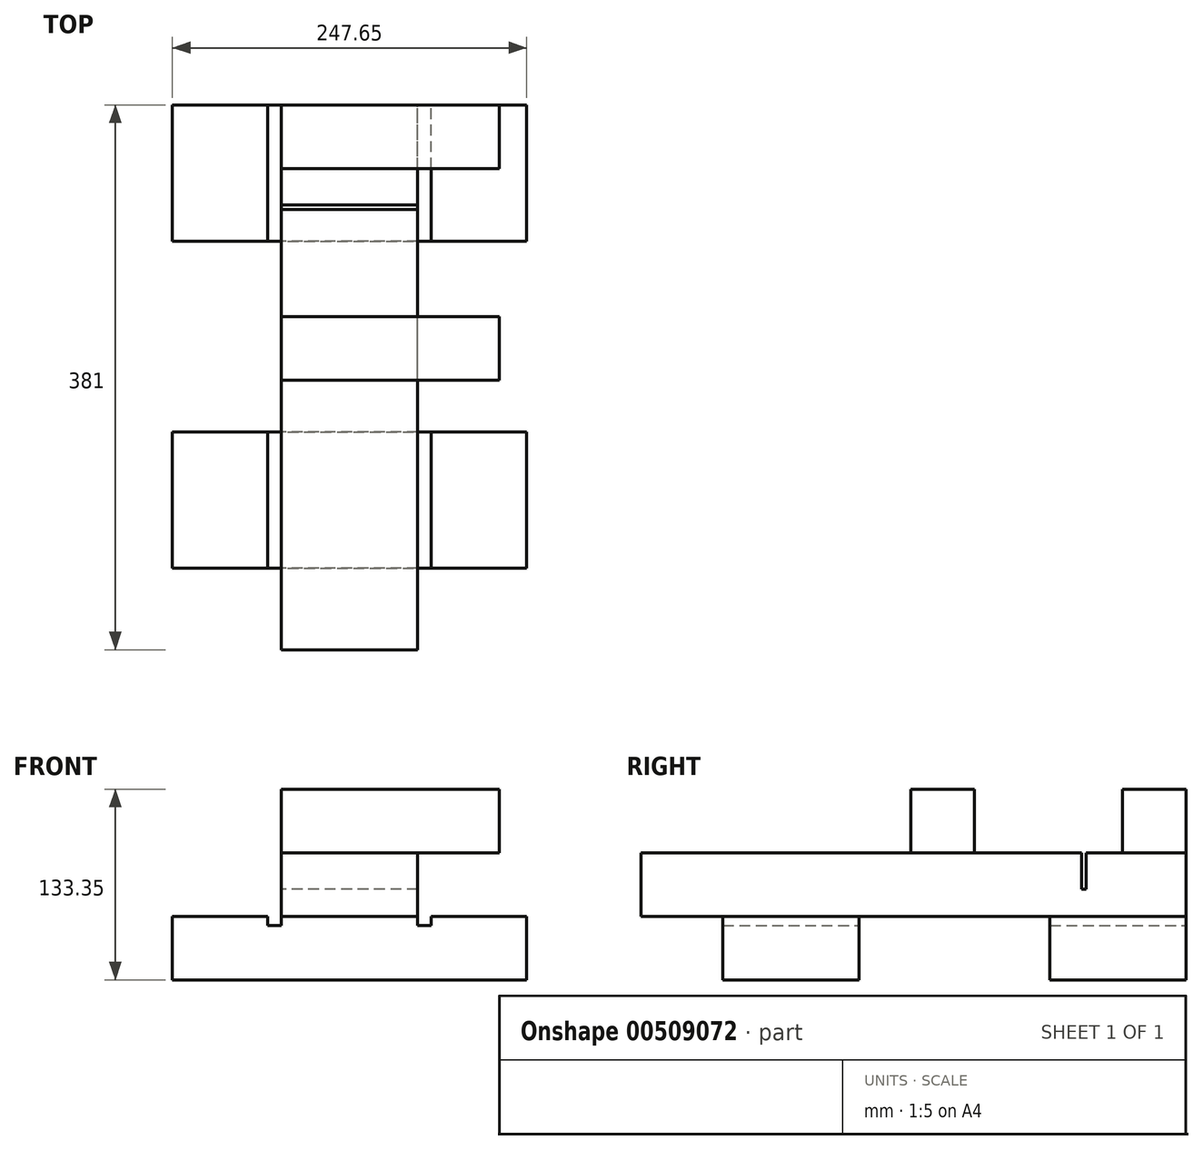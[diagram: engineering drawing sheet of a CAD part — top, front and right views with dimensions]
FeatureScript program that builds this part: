
annotation { "Feature Type Name" : "Feature", "Feature Type Description" : "" }
export const myFeature = defineFeature(function(context is Context, id is Id, definition is map)
    precondition{}
    {
        {
            var Q0;
            Q0=qCreatedBy(makeId("Front.planeOp"),FACE);
            var sketch = newSketch(context, id + "F0", { "sketchPlane" : qUnion([Q0])});
            skLineSegment(sketch, "E0.bottom", {"start": v(0, 0) * mm, "end": v(95.25, 0) * mm});
            skLineSegment(sketch, "E0.top", {"start": v(0, 44.45) * mm, "end": v(95.25, 44.45) * mm});
            skLineSegment(sketch, "E0.left", {"start": v(0, 0) * mm, "end": v(0, 44.45) * mm});
            skLineSegment(sketch, "E0.right", {"start": v(95.25, 0) * mm, "end": v(95.25, 44.45) * mm});
            skSolve(sketch);
        }
        {
            var Q0;
            Q0=makeQuery(id+"F0.imprint","IMPRINT",FACE,{"disambiguationData":[TD([[makeQuery(id+"F0.imprint","IMPRINT",EDGE,{"derivedFrom":sQuery(id+"F0.wireOp",EDGE,"E0.bottom")}),1.0]])]});
            extrude(context, id + "F1", {"entities" : qUnion([Q0]), "depth" : 381 * mm});
        }
        {
            var Q0;
            Q0=qCreatedBy(makeId("Front.planeOp"),FACE);
            var sketch = newSketch(context, id + "F2", { "sketchPlane" : qUnion([Q0])});
            skLineSegment(sketch, "E1", {"start": v(-9.52, 0) * mm, "end": v(-76.2, 0) * mm});
            skLineSegment(sketch, "E2", {"start": v(-76.2, 0) * mm, "end": v(-76.2, -44.45) * mm});
            skLineSegment(sketch, "E3", {"start": v(-76.2, -44.45) * mm, "end": v(171.45, -44.45) * mm});
            skLineSegment(sketch, "E4", {"start": v(171.45, -44.45) * mm, "end": v(171.45, 0) * mm});
            skLineSegment(sketch, "E5", {"start": v(171.45, 0) * mm, "end": v(104.78, 0) * mm});
            skLineSegment(sketch, "E6", {"start": v(104.78, 0) * mm, "end": v(104.78, -6.35) * mm});
            skLineSegment(sketch, "E7", {"start": v(104.78, -6.35) * mm, "end": v(95.25, -6.35) * mm});
            skLineSegment(sketch, "E8", {"start": v(95.25, -6.35) * mm, "end": v(95.25, 0) * mm});
            skLineSegment(sketch, "E9", {"start": v(95.25, 0) * mm, "end": v(0, 0) * mm});
            skLineSegment(sketch, "E10", {"start": v(0, 0) * mm, "end": v(0, -6.35) * mm});
            skLineSegment(sketch, "E11", {"start": v(0, -6.35) * mm, "end": v(-9.52, -6.35) * mm});
            skLineSegment(sketch, "E12", {"start": v(-9.52, -6.35) * mm, "end": v(-9.52, 0) * mm});
            skSolve(sketch);
        }
        {
            var Q0;
            Q0=makeQuery(id+"F2.imprint","IMPRINT",FACE,{"disambiguationData":[TD([[makeQuery(id+"F2.imprint","IMPRINT",EDGE,{"derivedFrom":sQuery(id+"F2.wireOp",EDGE,"E1")}),1.0]])]});
            extrude(context, id + "F3", {"entities" : qUnion([Q0]), "depth" : 95.25 * mm});
        }
        {
            var Q0;
            Q0=qCreatedBy(makeId("Front.planeOp"),FACE);
            cPlane(context, id + "F4", {"entities" : qUnion([Q0]), "cplaneType" : CPlaneType.OFFSET, "offset" : 228.6 * mm, "width" : 152.4 * mm, "height" : 152.4 * mm});
        }
        {
            var Q0;
            Q0=qCreatedBy(id+"F4.planeOp",FACE);
            var sketch = newSketch(context, id + "F5", { "sketchPlane" : qUnion([Q0])});
            skLineSegment(sketch, "E13", {"start": v(-9.53, 0) * mm, "end": v(-76.2, 0) * mm});
            skLineSegment(sketch, "E14", {"start": v(-76.2, 0) * mm, "end": v(-76.2, -44.45) * mm});
            skLineSegment(sketch, "E15", {"start": v(-76.2, -44.45) * mm, "end": v(171.45, -44.45) * mm});
            skLineSegment(sketch, "E16", {"start": v(171.45, -44.45) * mm, "end": v(171.45, 0) * mm});
            skLineSegment(sketch, "E17", {"start": v(171.45, 0) * mm, "end": v(104.78, 0) * mm});
            skLineSegment(sketch, "E18", {"start": v(104.78, 0) * mm, "end": v(104.78, -6.35) * mm});
            skLineSegment(sketch, "E19", {"start": v(104.78, -6.35) * mm, "end": v(95.25, -6.35) * mm});
            skLineSegment(sketch, "E20", {"start": v(95.25, -6.35) * mm, "end": v(95.25, 0) * mm});
            skLineSegment(sketch, "E21", {"start": v(95.25, 0) * mm, "end": v(0, 0) * mm});
            skLineSegment(sketch, "E22", {"start": v(0, 0) * mm, "end": v(0, -6.35) * mm});
            skLineSegment(sketch, "E23", {"start": v(0, -6.35) * mm, "end": v(-9.53, -6.35) * mm});
            skLineSegment(sketch, "E24", {"start": v(-9.53, -6.35) * mm, "end": v(-9.53, 0) * mm});
            skSolve(sketch);
        }
        {
            var Q0;
            Q0=makeQuery(id+"F5.imprint","IMPRINT",FACE,{"disambiguationData":[TD([[makeQuery(id+"F5.imprint","IMPRINT",EDGE,{"derivedFrom":sQuery(id+"F5.wireOp",EDGE,"E13")}),1.0]])]});
            extrude(context, id + "F6", {"entities" : qUnion([Q0]), "depth" : 95.25 * mm});
        }
        {
            var Q0;
            Q0=qCreatedBy(makeId("Right.planeOp"),FACE);
            var sketch = newSketch(context, id + "F7", { "sketchPlane" : qUnion([Q0])});
            skLineSegment(sketch, "E25.bottom", {"start": v(-192.53, 88.9) * mm, "end": v(-148.08, 88.9) * mm});
            skLineSegment(sketch, "E25.top", {"start": v(-192.53, 44.45) * mm, "end": v(-148.08, 44.45) * mm});
            skLineSegment(sketch, "E25.left", {"start": v(-192.53, 88.9) * mm, "end": v(-192.53, 44.45) * mm});
            skLineSegment(sketch, "E25.right", {"start": v(-148.08, 88.9) * mm, "end": v(-148.08, 44.45) * mm});
            skLineSegment(sketch, "E26.bottom", {"start": v(-44.45, 88.9) * mm, "end": v(0, 88.9) * mm});
            skLineSegment(sketch, "E26.top", {"start": v(-44.45, 44.45) * mm, "end": v(0, 44.45) * mm});
            skLineSegment(sketch, "E26.left", {"start": v(-44.45, 88.9) * mm, "end": v(-44.45, 44.45) * mm});
            skLineSegment(sketch, "E26.right", {"start": v(0, 88.9) * mm, "end": v(0, 44.45) * mm});
            skSolve(sketch);
        }
        {
            var Q0;
            Q0=makeQuery(id+"F7.imprint","IMPRINT",FACE,{"disambiguationData":[TD([[makeQuery(id+"F7.imprint","IMPRINT",EDGE,{"derivedFrom":sQuery(id+"F7.wireOp",EDGE,"E25.bottom")}),-1.0]])]});
            var Q1;
            Q1=makeQuery(id+"F7.imprint","IMPRINT",FACE,{"disambiguationData":[TD([[makeQuery(id+"F7.imprint","IMPRINT",EDGE,{"derivedFrom":sQuery(id+"F7.wireOp",EDGE,"E26.bottom")}),-1.0]])]});
            extrude(context, id + "F8", {"entities" : qUnion([Q0, Q1]), "depth" : 152.4 * mm});
        }
        {
            var Q0;
            Q0=qCreatedBy(makeId("Right.planeOp"),FACE);
            var sketch = newSketch(context, id + "F9", { "sketchPlane" : qUnion([Q0])});
            skLineSegment(sketch, "E27.bottom", {"start": v(-69.85, 44.45) * mm, "end": v(-73.02, 44.45) * mm});
            skLineSegment(sketch, "E27.top", {"start": v(-69.85, 19.05) * mm, "end": v(-73.02, 19.05) * mm});
            skLineSegment(sketch, "E27.left", {"start": v(-69.85, 44.45) * mm, "end": v(-69.85, 19.05) * mm});
            skLineSegment(sketch, "E27.right", {"start": v(-73.03, 44.45) * mm, "end": v(-73.03, 19.05) * mm});
            skSolve(sketch);
        }
        {
            var Q0;
            Q0=makeQuery(id+"F9.imprint","IMPRINT",FACE,{"disambiguationData":[TD([[makeQuery(id+"F9.imprint","IMPRINT",EDGE,{"derivedFrom":sQuery(id+"F9.wireOp",EDGE,"E27.bottom")}),1.0]])]});
            extrude(context, id + "F10", {"entities" : qUnion([Q0]), "operationType" : NewBodyOperationType.REMOVE, "endBound" : BoundingType.THROUGH_ALL, "depth" : 25.4 * mm});
        }
    });
